# Revit family: Lighting_Wall_Zero_Lumo
name_source: partatom
category: Lighting Fixtures
units: mm (PartAtom-declared; Revit-internal decimal feet)

## family parameters
Cut with Voids When Loaded = No
Host = Face
Light Source = Yes
OmniClass Number = 23.80.70.00
OmniClass Title = Lighting
Part Type = Normal
Room Calculation Point = No
Round Connector Dimension = Use Diameter
Shared = No

## types (2) — shared parameters
AssetType = Fixed
BIMObjectName = Lighting_Wall_Zero_Lumo
Brand = Zero
Category = Wall Fixtures
Color = Yellow
Color Filter = 16777215
Designer = Thomas Bernstrand 2023
Dimming Lamp Color Temperature Shift = <None>
DurationUnit = Years
Features = Can be ordered with diffuser in Masterpoint glass.
Finish = Painted die-cast aluminum in black RAL 9005. Diffuser in matt acrylic.
HasProtectiveEarth = Yes
IP_Code = IP44
IfcExportAs = IfcLightFixtureType
IfcExportType = NOTDEFINED
Lamp = Can be delivered with 2700K, 4000K on request.
LensMaterial = Glass
Light Source Symbol Length = 300 mm
LightFixtureMainMaterial = Black RAL 9005
LightFixtureMountingType = Surface
LightFixturePlacingType = Wall
LightOffsetX = 70 mm  [stored 0.229659 ft]
LightOffsetY = 137 mm
Manufacturer = Zero
ManufacturerName = Zero
ManufacturerURL = https://www.zerolighting.com
ManufacturersSpecificInformation = Terminal block 5x,2,5mm2
Material = Metal
NBSDescription = General purpose luminaires
NBSReference = 90-60-50/405
Name = Wall_Zero_Lumo
NominalCurrent = 0 A
NominalDiameter = 250 mm  [stored 0.82021 ft]
NominalFrequencyRange = 50 Hz
NominalHeight = 300 mm
NominalLength = 249 mm
NominalRadius = 125 mm  [stored 0.410105 ft]
NominalVoltage = 230 V
NominalVoltageCalc = 0 V
NominalWidth = 253 mm
NumberOfPoles = 1
PhaseAngle = 0.00°
Shape = Sculptured
Size = 253x250x300 mm
Spot Beam Angle = 90.00°
Spot Field Angle = 90.00°
Tilt Angle = 90.00°
TotalWattage = 0 W
Uniclass2 = 90-65-49/434
Uniclass2015Description = Suspended luminaires
Uniclass2015Reference = Pr_70_70_49_86
UsageCurrent = 0 A
Version = 1
VersionDate = 07.07.2023
WarrantyDurationUnit = Years
zero-valued in all types: Default Elevation, ElectricalDeviceNominalPower, MaintenanceFactor, NumberOfSources

## per-type parameters (varying)
| type | ArticleNumber | ModelNumber |
| Lumo wall - Black Matt acrylic, on/off | 12140106-30 | 12140106-30 |
| Lumo wall - Black Matt acrylic, Dali | 12140106D30 | 12140106D30 |

note: column(s) folded — value = type name in every type: Model

note: [stored X ft] marks values corroborated as IEEE doubles in the binary element streams (Revit-internal decimal feet)

## geometry (parser evidence)
native form markers: Sweep x7
no freeform markers — native parametric forms only
